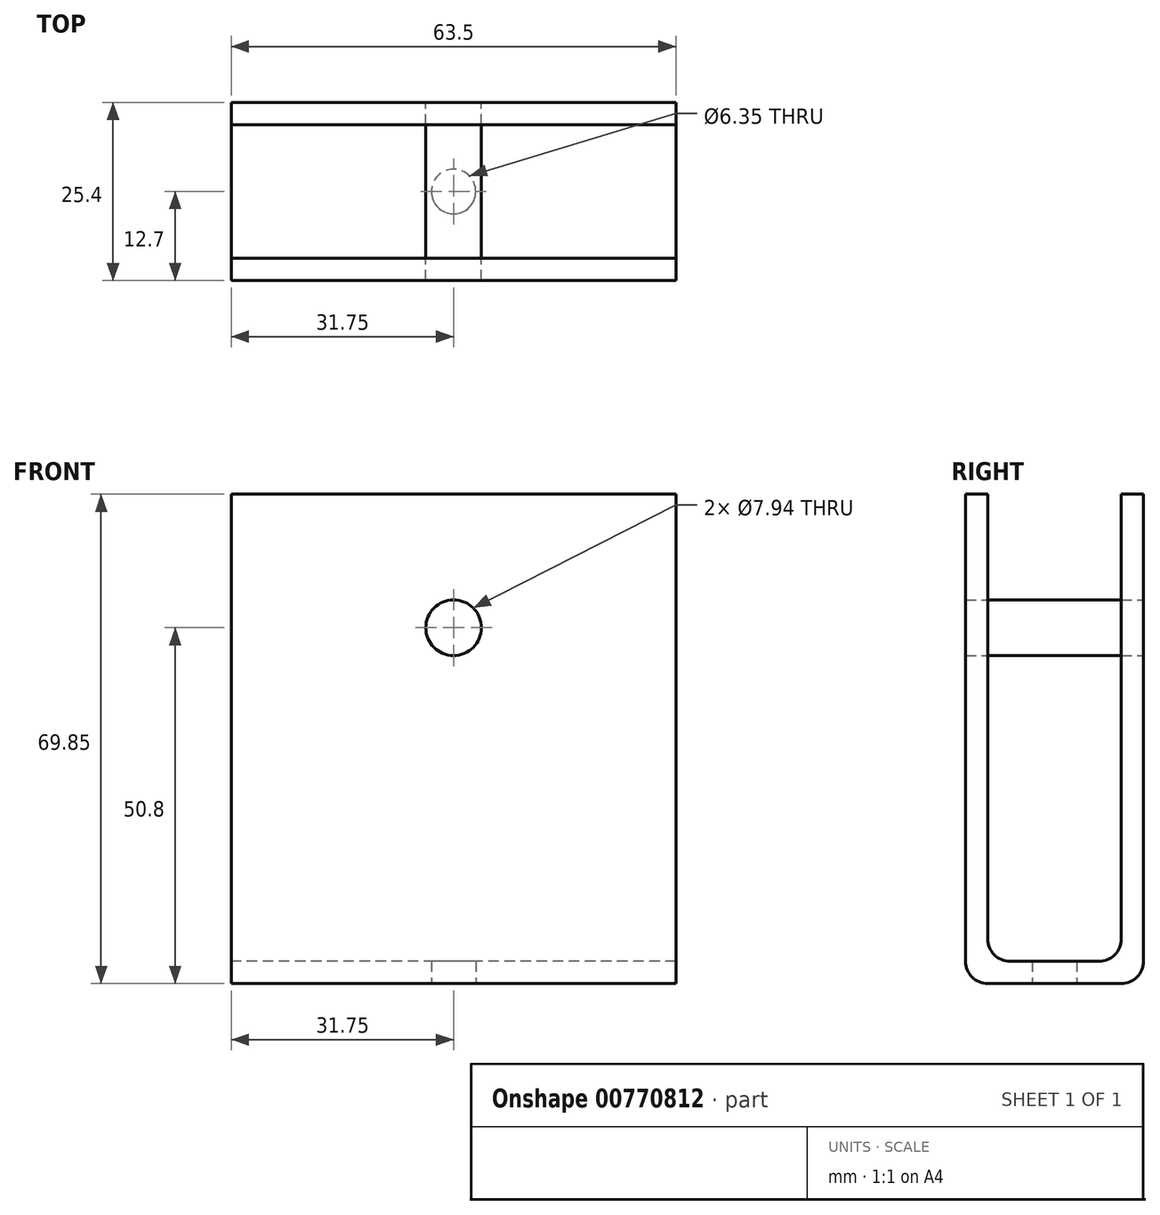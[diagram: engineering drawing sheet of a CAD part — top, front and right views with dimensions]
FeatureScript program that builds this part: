
annotation { "Feature Type Name" : "Feature", "Feature Type Description" : "" }
export const myFeature = defineFeature(function(context is Context, id is Id, definition is map)
    precondition{}
    {
        {
            var Q0;
            Q0=qCreatedBy(makeId("Right.planeOp"),FACE);
            var sketch = newSketch(context, id + "F0", { "sketchPlane" : qUnion([Q0])});
            skLineSegment(sketch, "E0.bottom", {"start": v(3.18, 0) * mm, "end": v(22.23, 0) * mm});
            skLineSegment(sketch, "E0.top", {"start": v(3.18, 76.2) * mm, "end": v(22.22, 76.2) * mm});
            skLineSegment(sketch, "E0.left", {"start": v(0, 3.18) * mm, "end": v(0, 73.03) * mm});
            skLineSegment(sketch, "E0.right", {"start": v(25.4, 3.18) * mm, "end": v(25.4, 73.03) * mm});
            skLineSegment(sketch, "E1.bottom", {"start": v(6.35, 3.18) * mm, "end": v(19.05, 3.18) * mm});
            skLineSegment(sketch, "E1.top", {"start": v(6.35, 73.03) * mm, "end": v(19.05, 73.03) * mm});
            skLineSegment(sketch, "E1.left", {"start": v(3.18, 6.35) * mm, "end": v(3.18, 69.85) * mm});
            skLineSegment(sketch, "E1.right", {"start": v(22.22, 6.35) * mm, "end": v(22.22, 69.85) * mm});
            skPoint(sketch, "E2.visualSharp", {"position": v(25.4, 76.2) * mm});
            skArc(sketch, "E2.filletArc", {"start": v(25.4, 73.03) * mm, "mid": v(24.47, 75.27) * mm, "end": v(22.22, 76.2) * mm});
            skPoint(sketch, "E3.visualSharp", {"position": v(25.4, 0) * mm});
            skArc(sketch, "E3.filletArc", {"start": v(22.23, 0) * mm, "mid": v(24.47, 0.93) * mm, "end": v(25.4, 3.18) * mm});
            skPoint(sketch, "E4.visualSharp", {"position": v(22.23, 3.18) * mm});
            skArc(sketch, "E4.filletArc", {"start": v(19.05, 3.18) * mm, "mid": v(21.3, 4.1) * mm, "end": v(22.22, 6.35) * mm});
            skPoint(sketch, "E5.visualSharp", {"position": v(3.18, 3.18) * mm});
            skArc(sketch, "E5.filletArc", {"start": v(3.18, 6.35) * mm, "mid": v(4.1, 4.1) * mm, "end": v(6.35, 3.18) * mm});
            skPoint(sketch, "E6.visualSharp", {"position": v(0, 0) * mm});
            skArc(sketch, "E6.filletArc", {"start": v(0, 3.18) * mm, "mid": v(0.93, 0.93) * mm, "end": v(3.18, 0) * mm});
            skPoint(sketch, "E7.visualSharp", {"position": v(3.18, 73.03) * mm});
            skArc(sketch, "E7.filletArc", {"start": v(6.35, 73.03) * mm, "mid": v(4.1, 72.1) * mm, "end": v(3.17, 69.85) * mm});
            skPoint(sketch, "E8.visualSharp", {"position": v(0, 76.2) * mm});
            skArc(sketch, "E8.filletArc", {"start": v(3.17, 76.2) * mm, "mid": v(0.93, 75.27) * mm, "end": v(0, 73.03) * mm});
            skArc(sketch, "E9.filletArc", {"start": v(22.22, 69.85) * mm, "mid": v(21.3, 72.1) * mm, "end": v(19.05, 73.03) * mm});
            skSolve(sketch);
        }
        {
            var Q0;
            Q0=makeQuery(id+"F0.imprint","IMPRINT",FACE,{"disambiguationData":[TD([[makeQuery(id+"F0.imprint","IMPRINT",EDGE,{"derivedFrom":sQuery(id+"F0.wireOp",EDGE,"E0.bottom")}),1.0]])]});
            extrude(context, id + "F1", {"entities" : qUnion([Q0]), "depth" : 63.5 * mm, "offsetDistance" : 25.4 * mm});
        }
        {
            var Q0;
            Q0=makeQuery(id+"F1.opExtrude","SWEPT_FACE",FACE,{"disambiguationData":[OSD([sQuery(id+"F0.wireOp",EDGE,"E0.left")])]});
            var sketch = newSketch(context, id + "F2", { "sketchPlane" : qUnion([Q0])});
            skLineSegment(sketch, "E10.0", {"start": v(63.5, 76.2) * mm, "end": v(0, 76.2) * mm});
            skLineSegment(sketch, "E11.0", {"start": v(0, 76.2) * mm, "end": v(0, 73.03) * mm});
            skLineSegment(sketch, "E12.0", {"start": v(63.5, 76.2) * mm, "end": v(63.5, 73.03) * mm});
            skLineSegment(sketch, "E13", {"start": v(0, 76.2) * mm, "end": v(0, 69.85) * mm});
            skLineSegment(sketch, "E14", {"start": v(0, 69.85) * mm, "end": v(63.5, 69.85) * mm});
            skLineSegment(sketch, "E15", {"start": v(63.5, 69.85) * mm, "end": v(63.5, 76.2) * mm});
            skSolve(sketch);
        }
        {
            var Q0;
            {var subQ3=sQuery(id+"F2.wireOp",EDGE,"E14");Q0=makeQuery(id+"F2.imprint","IMPRINT",FACE,{"disambiguationData":[TD([[makeQuery(id+"F2.imprint","IMPRINT",EDGE,{"derivedFrom":subQ3}),1.0]])]});}
            var Q1;
            {var subQ0=sQuery(id+"F2.wireOp",EDGE,"E10.0");Q1=makeQuery(id+"F2.imprint","IMPRINT",FACE,{"disambiguationData":[TD([[makeQuery(id+"F2.imprint","IMPRINT",EDGE,{"derivedFrom":subQ0}),1.0]])]});}
            extrude(context, id + "F3", {"entities" : qUnion([Q0, Q1]), "operationType" : NewBodyOperationType.REMOVE, "endBound" : BoundingType.THROUGH_ALL, "oppositeDirection" : true, "depth" : 25.4 * mm, "offsetDistance" : 25.4 * mm});
        }
        {
            var Q0;
            Q0=makeQuery(id+"F1.opExtrude","SWEPT_FACE",FACE,{"disambiguationData":[OSD([sQuery(id+"F0.wireOp",EDGE,"E0.left")])]});
            var sketch = newSketch(context, id + "F4", { "sketchPlane" : qUnion([Q0])});
            skLineSegment(sketch, "E16.0", {"start": v(63.5, 0) * mm, "end": v(0, 0) * mm});
            skCircle(sketch, "E17", {"center": v(31.75, 50.8) * mm, "radius": 3.97 * mm});
            skSolve(sketch);
        }
        {
            var Q0;
            Q0=makeQuery(id+"F4.imprint","IMPRINT",FACE,{"disambiguationData":[TD([[makeQuery(id+"F4.imprint","IMPRINT",EDGE,{"derivedFrom":sQuery(id+"F4.wireOp",EDGE,"E17")}),1.0]])]});
            extrude(context, id + "F5", {"entities" : qUnion([Q0]), "operationType" : NewBodyOperationType.REMOVE, "endBound" : BoundingType.THROUGH_ALL, "oppositeDirection" : true, "depth" : 25.4 * mm, "offsetDistance" : 25.4 * mm});
        }
        {
            var Q0;
            Q0=makeQuery(id+"F1.opExtrude","SWEPT_FACE",FACE,{"disambiguationData":[OSD([sQuery(id+"F0.wireOp",EDGE,"E0.bottom")])]});
            var sketch = newSketch(context, id + "F6", { "sketchPlane" : qUnion([Q0])});
            skCircle(sketch, "E18", {"center": v(31.75, -12.7) * mm, "radius": 3.18 * mm});
            skLineSegment(sketch, "E19", {"start": v(31.75, -3.18) * mm, "end": v(31.75, -22.23) * mm, "construction": true});
            skLineSegment(sketch, "E20", {"start": v(0, -12.7) * mm, "end": v(63.5, -12.7) * mm, "construction": true});
            skSolve(sketch);
        }
        {
            var Q0;
            Q0=makeQuery(id+"F6.imprint","IMPRINT",FACE,{"disambiguationData":[TD([[makeQuery(id+"F6.imprint","IMPRINT",EDGE,{"derivedFrom":sQuery(id+"F6.wireOp",EDGE,"E18")}),1.0]])]});
            extrude(context, id + "F7", {"entities" : qUnion([Q0]), "operationType" : NewBodyOperationType.REMOVE, "endBound" : BoundingType.THROUGH_ALL, "oppositeDirection" : true, "depth" : 25.4 * mm, "offsetDistance" : 25.4 * mm});
        }
        {
            var Q0;
            Q0=makeQuery(id+"F1.opExtrude","SWEPT_FACE",FACE,{"disambiguationData":[OSD([sQuery(id+"F0.wireOp",EDGE,"E0.right")])]});
            var sketch = newSketch(context, id + "F8", { "sketchPlane" : qUnion([Q0])});
            skCircle(sketch, "E21.0", {"center": v(-31.75, 50.8) * mm, "radius": 3.97 * mm});
            skSolve(sketch);
        }
        {
            var Q0;
            Q0=makeQuery(id+"F8.imprint","IMPRINT",FACE,{"disambiguationData":[TD([[makeQuery(id+"F8.imprint","IMPRINT",EDGE,{"derivedFrom":sQuery(id+"F8.wireOp",EDGE,"E21.0")}),-1.0]])]});
            extrude(context, id + "F9", {"entities" : qUnion([Q0]), "oppositeDirection" : true, "depth" : 25.4 * mm, "offsetDistance" : 25.4 * mm});
        }
    });
